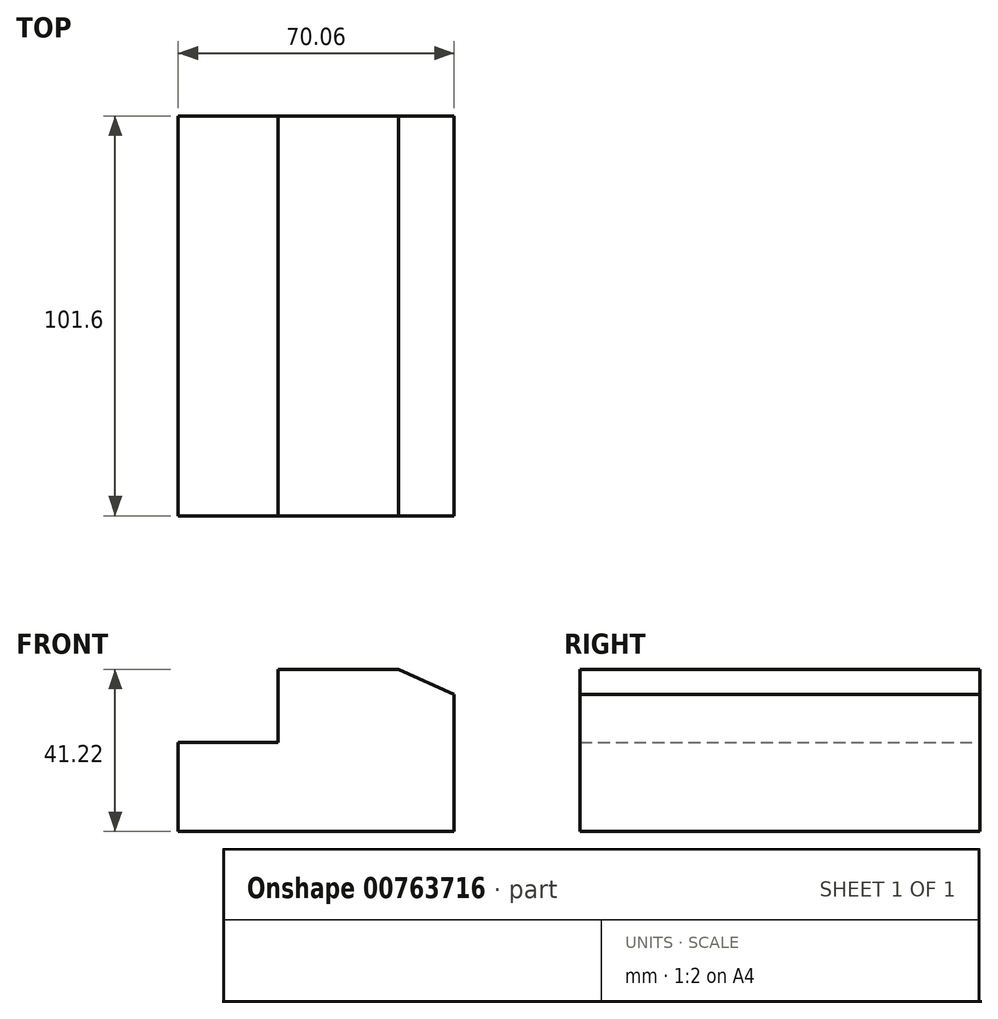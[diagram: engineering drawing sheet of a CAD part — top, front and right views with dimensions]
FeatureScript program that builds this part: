
annotation { "Feature Type Name" : "Feature", "Feature Type Description" : "" }
export const myFeature = defineFeature(function(context is Context, id is Id, definition is map)
    precondition{}
    {
        {
            var Q0;
            Q0=qCreatedBy(makeId("Front.planeOp"),FACE);
            var sketch = newSketch(context, id + "F0", { "sketchPlane" : qUnion([Q0])});
            skLineSegment(sketch, "E0", {"start": v(0, 0) * mm, "end": v(0, 22.6) * mm});
            skLineSegment(sketch, "E1", {"start": v(0, 22.6) * mm, "end": v(25.4, 22.6) * mm});
            skLineSegment(sketch, "E2", {"start": v(25.4, 22.6) * mm, "end": v(25.4, 41.22) * mm});
            skLineSegment(sketch, "E3", {"start": v(25.4, 41.22) * mm, "end": v(55.92, 41.22) * mm});
            skLineSegment(sketch, "E4", {"start": v(55.92, 41.22) * mm, "end": v(70.06, 34.9) * mm});
            skLineSegment(sketch, "E5", {"start": v(70.06, 34.9) * mm, "end": v(70.06, 0) * mm});
            skLineSegment(sketch, "E6", {"start": v(70.06, 0) * mm, "end": v(0, 0) * mm});
            skSolve(sketch);
        }
        {
            var Q0;
            Q0=makeQuery(id+"F0.imprint","IMPRINT",FACE,{"disambiguationData":[TD([[makeQuery(id+"F0.imprint","IMPRINT",EDGE,{"derivedFrom":sQuery(id+"F0.wireOp",EDGE,"E0")}),-1.0]])]});
            extrude(context, id + "F1", {"entities" : qUnion([Q0]), "depth" : 101.6 * mm, "offsetDistance" : 25.4 * mm});
        }
    });
